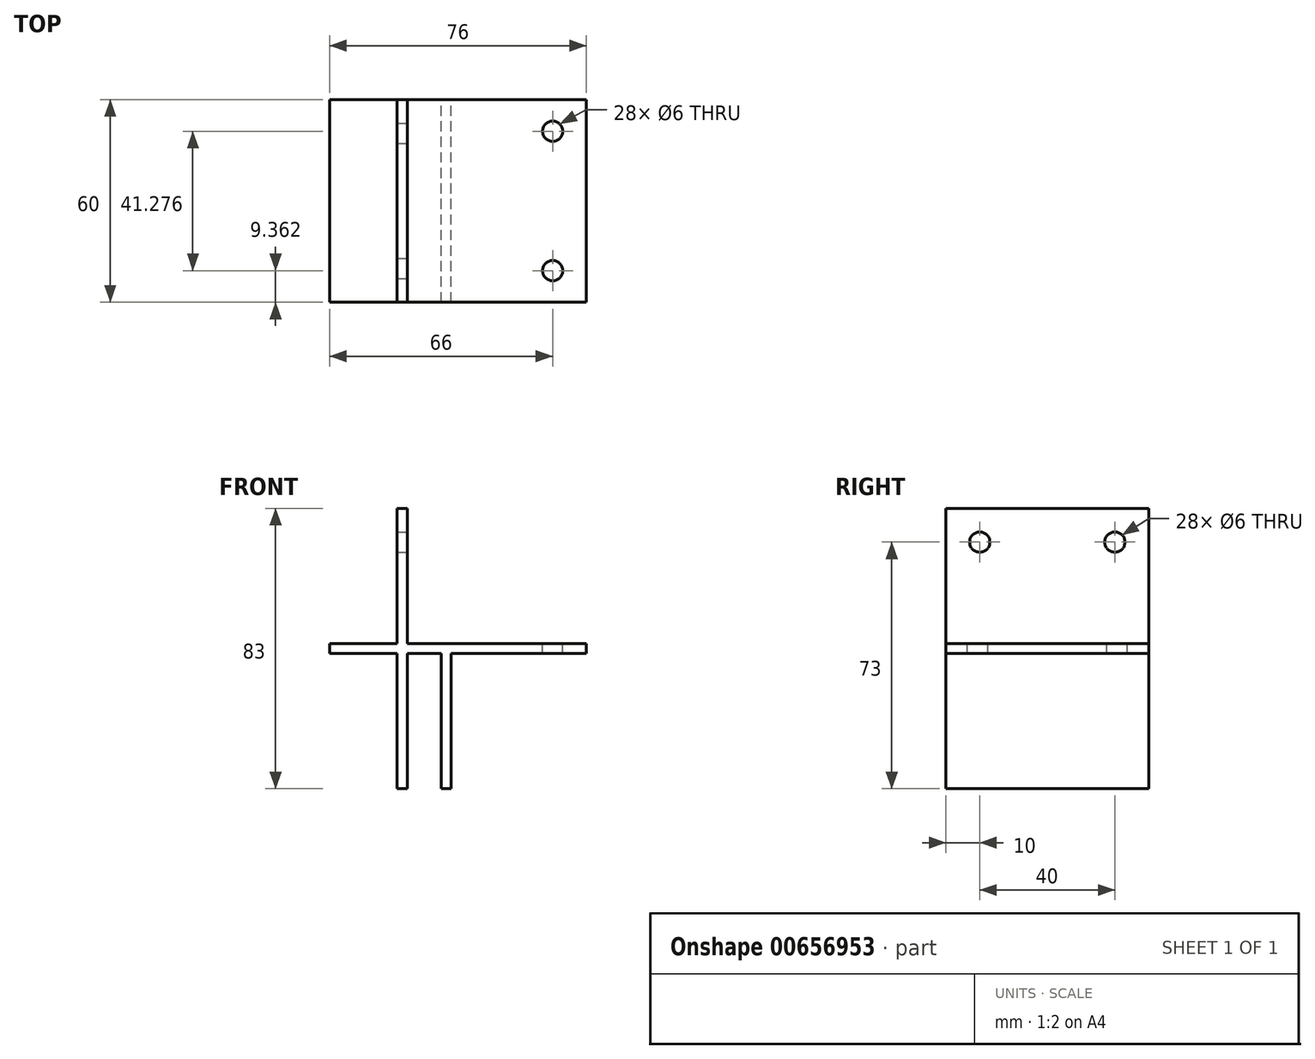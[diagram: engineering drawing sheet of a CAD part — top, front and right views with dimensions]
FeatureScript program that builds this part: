
annotation { "Feature Type Name" : "Feature", "Feature Type Description" : "" }
export const myFeature = defineFeature(function(context is Context, id is Id, definition is map)
    precondition{}
    {
        {
            var Q0;
            Q0=qCreatedBy(makeId("Front.planeOp"),FACE);
            var sketch = newSketch(context, id + "F0", { "sketchPlane" : qUnion([Q0])});
            skLineSegment(sketch, "E0.bottom", {"start": v(-1.5, 41.5) * mm, "end": v(1.5, 41.5) * mm});
            skLineSegment(sketch, "E0.top", {"start": v(-1.5, -41.5) * mm, "end": v(1.5, -41.5) * mm});
            skLineSegment(sketch, "E0.left", {"start": v(-1.5, 41.5) * mm, "end": v(-1.5, -41.5) * mm});
            skLineSegment(sketch, "E0.right", {"start": v(1.5, 41.5) * mm, "end": v(1.5, -41.5) * mm});
            skPoint(sketch, "E0.middle", {"position": v(0, 0) * mm});
            skLineSegment(sketch, "E1.bottom", {"start": v(-21.5, 1.5) * mm, "end": v(21.5, 1.5) * mm});
            skLineSegment(sketch, "E1.top", {"start": v(-21.5, -1.5) * mm, "end": v(21.5, -1.5) * mm});
            skLineSegment(sketch, "E1.left", {"start": v(-21.5, 1.5) * mm, "end": v(-21.5, -1.5) * mm});
            skLineSegment(sketch, "E2.left", {"start": v(14.5, -8.77) * mm, "end": v(14.5, 1.5) * mm});
            skLineSegment(sketch, "E2.right", {"start": v(11.5, -8.77) * mm, "end": v(11.5, 1.5) * mm});
            skPoint(sketch, "E2.middle", {"position": v(13, 0) * mm});
            skLineSegment(sketch, "E3.top", {"start": v(11.5, -41.5) * mm, "end": v(14.5, -41.5) * mm});
            skLineSegment(sketch, "E3.left", {"start": v(11.5, -8.77) * mm, "end": v(11.5, -41.5) * mm});
            skLineSegment(sketch, "E3.right", {"start": v(14.5, -8.77) * mm, "end": v(14.5, -41.5) * mm});
            skLineSegment(sketch, "E4.bottom", {"start": v(21.5, 1.5) * mm, "end": v(54.5, 1.5) * mm});
            skLineSegment(sketch, "E4.top", {"start": v(21.5, -1.5) * mm, "end": v(54.5, -1.5) * mm});
            skLineSegment(sketch, "E4.left", {"start": v(21.5, 1.5) * mm, "end": v(21.5, -1.5) * mm});
            skLineSegment(sketch, "E4.right", {"start": v(54.5, 1.5) * mm, "end": v(54.5, -1.5) * mm});
            skSolve(sketch);
        }
        {
            var Q0;
            Q0 = qSketchRegion(id + "F0", true);
            extrude(context, id + "F1", {"entities" : qUnion([Q0]), "depth" : 30 * mm, "offsetDistance" : 25 * mm, "hasSecondDirection" : true, "secondDirectionOppositeDirection" : true, "secondDirectionDepth" : 30 * mm});
        }
        {
            var Q0;
            {var subQ0=sQuery(id+"F0.wireOp",EDGE,"E0.right");Q0=makeQuery(id+"F1.opExtrude","SWEPT_FACE",FACE,{"disambiguationData":[OSD([subQ0]),TDD([makeQuery(id+"F0.imprint","IMPRINT",EDGE,{"disambiguationData":[TD([[makeQuery(id+"F0.imprint","INTERSECT",VERTEX,{"derivedFrom":[sQuery(id+"F0.wireOp",EDGE,"E0.bottom"),subQ0]}),-1.0]])],"derivedFrom":subQ0})])]});}
            var sketch = newSketch(context, id + "F2", { "sketchPlane" : qUnion([Q0])});
            skLineSegment(sketch, "E5", {"start": v(-30, 31.5) * mm, "end": v(30, 31.5) * mm, "construction": true});
            skCircle(sketch, "E6", {"center": v(-20, 31.5) * mm, "radius": 3 * mm});
            skLineSegment(sketch, "E7", {"start": v(0, 41.5) * mm, "end": v(0, 0) * mm, "construction": true});
            skCircle(sketch, "E8.MirrorC", {"center": v(20, 31.5) * mm, "radius": 3 * mm});
            skSolve(sketch);
        }
        {
            var Q0;
            Q0=sQuery(id+"F2.wireOp",VERTEX,"E6.center");
            var Q1;
            Q1=sQuery(id+"F2.wireOp",VERTEX,"E8.MirrorC.center");
            var Q2;
            Q2=makeQuery(id+"F1.opExtrude","SWEPT_BODY",BODY,{"disambiguationData":[OSD([sQuery(id+"F0.wireOp",EDGE,"E0.bottom"),sQuery(id+"F0.wireOp",EDGE,"E0.top"),sQuery(id+"F0.wireOp",EDGE,"E0.left"),sQuery(id+"F0.wireOp",EDGE,"E0.right"),sQuery(id+"F0.wireOp",EDGE,"E1.bottom"),sQuery(id+"F0.wireOp",EDGE,"E1.top"),sQuery(id+"F0.wireOp",EDGE,"E1.left"),sQuery(id+"F0.wireOp",EDGE,"E2.left"),sQuery(id+"F0.wireOp",EDGE,"E2.right"),sQuery(id+"F0.wireOp",EDGE,"E3.top"),sQuery(id+"F0.wireOp",EDGE,"E3.left"),sQuery(id+"F0.wireOp",EDGE,"E3.right"),sQuery(id+"F0.wireOp",EDGE,"E4.bottom"),sQuery(id+"F0.wireOp",EDGE,"E4.top"),sQuery(id+"F0.wireOp",EDGE,"E4.right")])]});
            hole(context, id + "F3", {"style" : HoleStyle.SIMPLE, "endStyle" : HoleEndStyle.BLIND, "holeDiameter" : 6 * mm, "majorDiameter" : 5 * mm, "holeDepth" : 12 * mm, "isTappedThrough" : true, "tappedDepth" : 12 * mm, "tapClearance" : 3, "locations" : qUnion([Q0, Q1]), "scope" : qUnion([Q2])});
        }
        {
            var Q0;
            Q0=makeQuery(id+"F1.opExtrude","SWEPT_FACE",FACE,{"disambiguationData":[OSD([sQuery(id+"F0.wireOp",EDGE,"E1.bottom"),sQuery(id+"F0.wireOp",EDGE,"E4.bottom")])]});
            var sketch = newSketch(context, id + "F4", { "sketchPlane" : qUnion([Q0])});
            skLineSegment(sketch, "E9", {"start": v(44.5, -30) * mm, "end": v(44.5, 30) * mm, "construction": true});
            skCircle(sketch, "E10", {"center": v(44.5, 20.64) * mm, "radius": 3 * mm});
            skLineSegment(sketch, "E11", {"start": v(0, 0) * mm, "end": v(54.5, 0) * mm, "construction": true});
            skCircle(sketch, "E12.MirrorC", {"center": v(44.5, -20.64) * mm, "radius": 3 * mm});
            skSolve(sketch);
        }
        {
            var Q0;
            Q0=sQuery(id+"F4.wireOp",VERTEX,"E10.center");
            var Q1;
            Q1=sQuery(id+"F4.wireOp",VERTEX,"E12.MirrorC.center");
            var Q2;
            Q2=makeQuery(id+"F1.opExtrude","SWEPT_BODY",BODY,{"disambiguationData":[OSD([sQuery(id+"F0.wireOp",EDGE,"E0.bottom"),sQuery(id+"F0.wireOp",EDGE,"E0.top"),sQuery(id+"F0.wireOp",EDGE,"E0.left"),sQuery(id+"F0.wireOp",EDGE,"E0.right"),sQuery(id+"F0.wireOp",EDGE,"E1.bottom"),sQuery(id+"F0.wireOp",EDGE,"E1.top"),sQuery(id+"F0.wireOp",EDGE,"E1.left"),sQuery(id+"F0.wireOp",EDGE,"E2.left"),sQuery(id+"F0.wireOp",EDGE,"E2.right"),sQuery(id+"F0.wireOp",EDGE,"E3.top"),sQuery(id+"F0.wireOp",EDGE,"E3.left"),sQuery(id+"F0.wireOp",EDGE,"E3.right"),sQuery(id+"F0.wireOp",EDGE,"E4.bottom"),sQuery(id+"F0.wireOp",EDGE,"E4.top"),sQuery(id+"F0.wireOp",EDGE,"E4.right")])]});
            hole(context, id + "F5", {"style" : HoleStyle.SIMPLE, "endStyle" : HoleEndStyle.BLIND, "holeDiameter" : 6 * mm, "majorDiameter" : 5 * mm, "holeDepth" : 12 * mm, "isTappedThrough" : true, "tappedDepth" : 12 * mm, "tapClearance" : 3, "locations" : qUnion([Q0, Q1]), "scope" : qUnion([Q2])});
        }
    });
